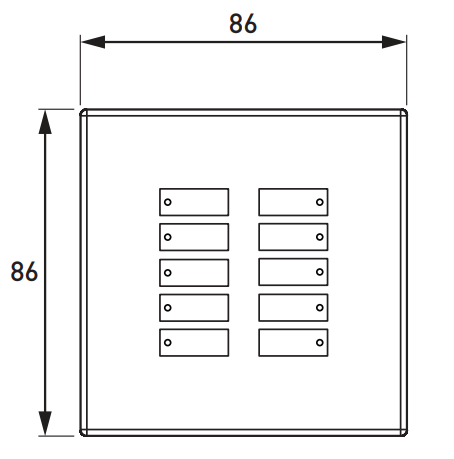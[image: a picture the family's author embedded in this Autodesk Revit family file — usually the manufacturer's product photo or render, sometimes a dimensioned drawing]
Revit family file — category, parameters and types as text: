
# Revit family: Enocean Panel _181X
name_source: partatom
category: Electrical Fixtures
revit_build: Autodesk Revit 2018 (Build: 20170223_1515(x64)
units: mm (PartAtom-declared; Revit-internal decimal feet)

## family parameters
Always vertical = Yes
Cut with Voids When Loaded = No
Maintain Annotation Orientation = No
Part Type = Normal
Room Calculation Point = No
Round Connector Dimension = Use Diameter
Shared = No
Work Plane-Based = Yes

## types (1)
- Single Rocker Switch_Black/White
    Ambient temperature = 0 °C to +50 °C
    Connections = No wiring (power or communications) is required
    Default Elevation = 0 mm  [stored 0 ft]
    Dimensions = 86 mm × 86 mm × 15 mm
    Environment = Complies with WEEE and RoHS directives.
    Frame = Stainless steel
    IP code = IP30
    Manufacturer = Helvar
    Material: = Switch rockers: plastic
    Max. No. of switch panels per gateway = 20
    Model = 181B/181W
    Mounting = Mount to back box, or mount on glass or flat surface
    Operating frequency = 868 MHz ISM band (Europe)
    Power = Signal power is generated by pressing the EnOcean button.
    RED 2014/53/EU = EN 301489-3, EN 300220-2
    Range: = 30 m (unobstructed space)
    Relative humidity = Max. 90 %, noncondensing
    Safety = EN 60950-1
    Storage temperature = –10 °C to +70 °C
    Switch colour = 18xW: white 18xB: black
    Weight = 150 g
    Wireless protocol = ISO/IEC 14543–3–10

note: [stored X ft] marks values corroborated as IEEE doubles in the binary element streams (Revit-internal decimal feet)

## geometry (parser evidence)
native form markers: Sweep x12
no freeform markers — native parametric forms only
